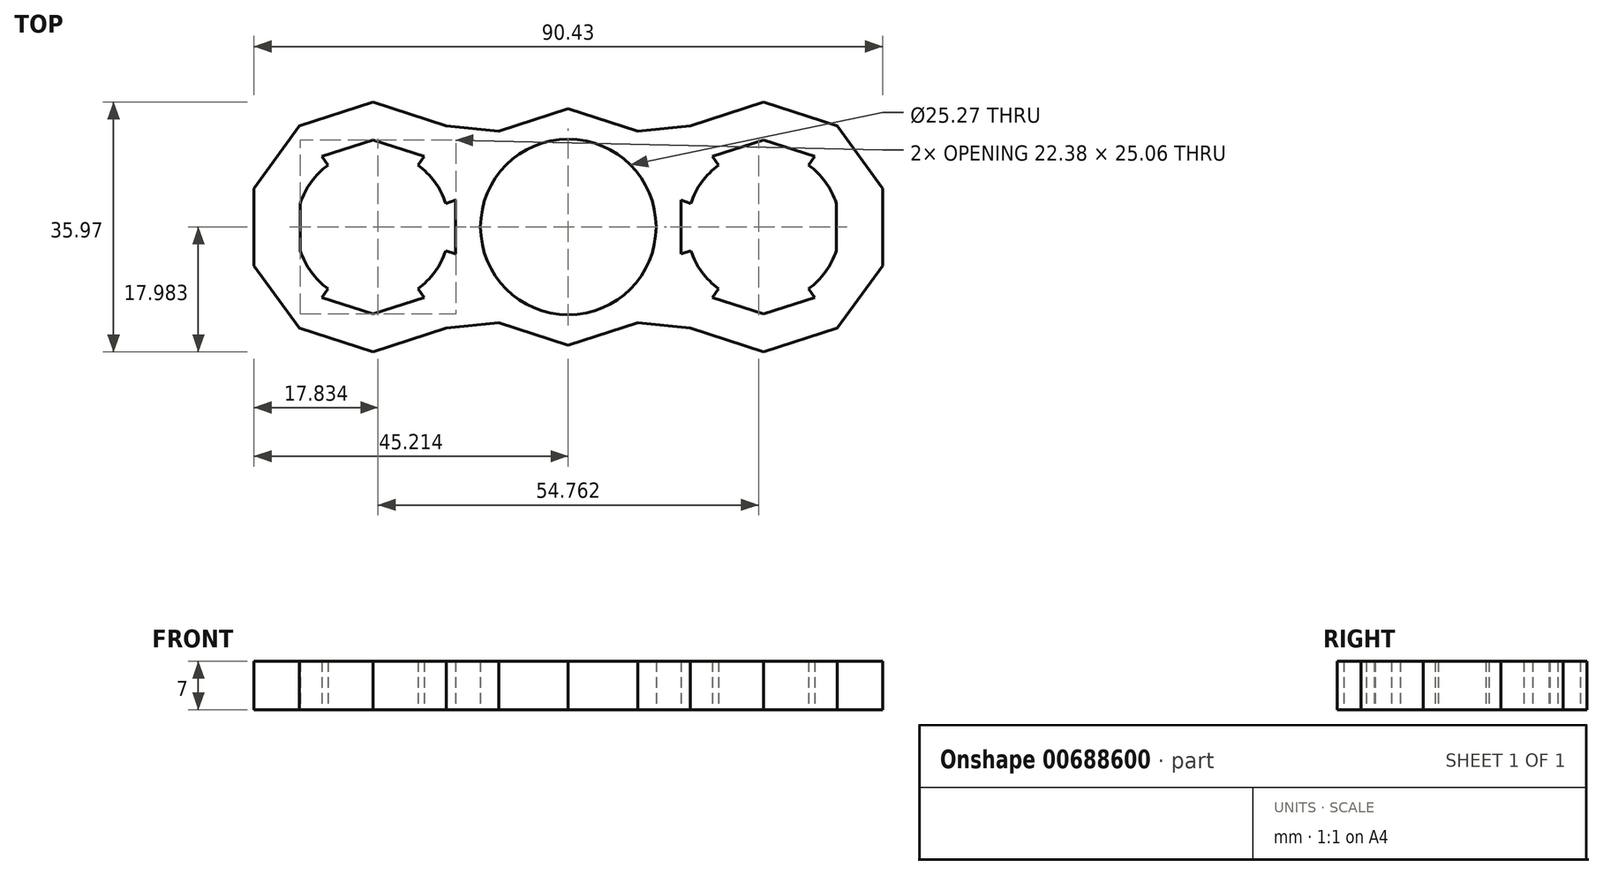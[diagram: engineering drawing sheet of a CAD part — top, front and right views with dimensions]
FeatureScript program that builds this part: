
annotation { "Feature Type Name" : "Feature", "Feature Type Description" : "" }
export const myFeature = defineFeature(function(context is Context, id is Id, definition is map)
    precondition{}
    {
        {
            var Q0;
            Q0=qCreatedBy(makeId("Top.planeOp"),FACE);
            var sketch = newSketch(context, id + "F0", { "sketchPlane" : qUnion([Q0])});
            skLineSegment(sketch, "E0.2", {"start": v(-42.82, -39.05) * mm, "end": v(-52.83, -42.3) * mm});
            skLineSegment(sketch, "E0.3", {"start": v(-52.83, -42.3) * mm, "end": v(-62.83, -39.05) * mm});
            skLineSegment(sketch, "E0.7", {"start": v(-62.83, -11.5) * mm, "end": v(-52.83, -8.25) * mm});
            skLineSegment(sketch, "E0.8", {"start": v(-52.83, -8.25) * mm, "end": v(-42.82, -11.5) * mm});
            skPoint(sketch, "E0.0.midPoint", {"position": v(-36.63, -25.28) * mm});
            skPoint(sketch, "E1.middle", {"position": v(-52.83, -25.28) * mm});
            skLineSegment(sketch, "E2.2", {"start": v(-70.36, -39.83) * mm, "end": v(-80.93, -43.26) * mm});
            skLineSegment(sketch, "E2.3", {"start": v(-80.93, -43.26) * mm, "end": v(-91.5, -39.83) * mm});
            skLineSegment(sketch, "E2.4", {"start": v(-91.5, -39.83) * mm, "end": v(-98.04, -30.84) * mm});
            skLineSegment(sketch, "E2.5", {"start": v(-98.04, -30.84) * mm, "end": v(-98.04, -19.72) * mm});
            skLineSegment(sketch, "E2.6", {"start": v(-98.04, -19.72) * mm, "end": v(-91.5, -10.72) * mm});
            skLineSegment(sketch, "E2.7", {"start": v(-91.5, -10.72) * mm, "end": v(-80.93, -7.29) * mm});
            skLineSegment(sketch, "E2.8", {"start": v(-80.93, -7.29) * mm, "end": v(-70.36, -10.72) * mm});
            skLineSegment(sketch, "E3.2", {"start": v(-35.3, -10.72) * mm, "end": v(-24.72, -7.29) * mm});
            skLineSegment(sketch, "E3.3", {"start": v(-24.72, -7.29) * mm, "end": v(-14.15, -10.72) * mm});
            skLineSegment(sketch, "E3.4", {"start": v(-14.15, -10.72) * mm, "end": v(-7.61, -19.72) * mm});
            skLineSegment(sketch, "E3.5", {"start": v(-7.61, -19.72) * mm, "end": v(-7.61, -30.84) * mm});
            skLineSegment(sketch, "E3.6", {"start": v(-7.61, -30.84) * mm, "end": v(-14.15, -39.83) * mm});
            skLineSegment(sketch, "E3.7", {"start": v(-14.15, -39.83) * mm, "end": v(-24.72, -43.26) * mm});
            skLineSegment(sketch, "E3.8", {"start": v(-24.72, -43.26) * mm, "end": v(-35.3, -39.83) * mm});
            skLineSegment(sketch, "E4", {"start": v(-42.82, -11.5) * mm, "end": v(-35.3, -10.72) * mm});
            skLineSegment(sketch, "E5", {"start": v(-70.36, -10.72) * mm, "end": v(-62.83, -11.5) * mm});
            skLineSegment(sketch, "E6", {"start": v(-70.36, -39.83) * mm, "end": v(-62.83, -39.05) * mm});
            skLineSegment(sketch, "E7", {"start": v(-42.82, -39.05) * mm, "end": v(-35.3, -39.83) * mm});
            skLineSegment(sketch, "E8.2", {"start": v(-73.57, -35.41) * mm, "end": v(-80.93, -37.8) * mm});
            skLineSegment(sketch, "E8.3", {"start": v(-80.93, -37.8) * mm, "end": v(-88.3, -35.41) * mm});
            skLineSegment(sketch, "E8.7", {"start": v(-88.3, -15.14) * mm, "end": v(-80.93, -12.75) * mm});
            skLineSegment(sketch, "E8.8", {"start": v(-80.93, -12.75) * mm, "end": v(-73.57, -15.14) * mm});
            skPoint(sketch, "E8.0.midPoint", {"position": v(-69.02, -25.28) * mm});
            skLineSegment(sketch, "E9", {"start": v(-70.47, -21.88) * mm, "end": v(-69.02, -21.4) * mm});
            skLineSegment(sketch, "E10", {"start": v(-70.47, -28.68) * mm, "end": v(-69.02, -29.15) * mm});
            skLineSegment(sketch, "E11.2", {"start": v(-32.08, -15.14) * mm, "end": v(-24.72, -12.75) * mm});
            skLineSegment(sketch, "E11.3", {"start": v(-24.72, -12.75) * mm, "end": v(-17.35, -15.14) * mm});
            skLineSegment(sketch, "E11.7", {"start": v(-17.35, -35.41) * mm, "end": v(-24.72, -37.8) * mm});
            skLineSegment(sketch, "E11.8", {"start": v(-24.72, -37.8) * mm, "end": v(-32.08, -35.41) * mm});
            skLineSegment(sketch, "E12", {"start": v(-36.63, -21.4) * mm, "end": v(-35.18, -21.88) * mm});
            skLineSegment(sketch, "E13", {"start": v(-36.63, -29.15) * mm, "end": v(-35.18, -28.68) * mm});
            skLineSegment(sketch, "E14", {"start": v(-69.02, -21.4) * mm, "end": v(-69.02, -29.15) * mm});
            skLineSegment(sketch, "E15", {"start": v(-74.47, -34.18) * mm, "end": v(-73.57, -35.41) * mm});
            skLineSegment(sketch, "E16", {"start": v(-87.4, -34.18) * mm, "end": v(-88.3, -35.41) * mm});
            skLineSegment(sketch, "E17", {"start": v(-87.4, -16.38) * mm, "end": v(-88.3, -15.14) * mm});
            skLineSegment(sketch, "E18", {"start": v(-74.47, -16.38) * mm, "end": v(-73.57, -15.14) * mm});
            skLineSegment(sketch, "E19", {"start": v(-36.63, -21.4) * mm, "end": v(-36.63, -29.15) * mm});
            skLineSegment(sketch, "E20", {"start": v(-32.08, -15.14) * mm, "end": v(-31.18, -16.38) * mm});
            skLineSegment(sketch, "E21", {"start": v(-17.35, -15.14) * mm, "end": v(-18.25, -16.38) * mm});
            skLineSegment(sketch, "E22", {"start": v(-18.25, -34.18) * mm, "end": v(-17.35, -35.41) * mm});
            skLineSegment(sketch, "E23", {"start": v(-31.18, -34.18) * mm, "end": v(-32.08, -35.41) * mm});
            skCircle(sketch, "E24", {"center": v(-52.83, -25.28) * mm, "radius": 12.64 * mm});
            skLineSegment(sketch, "E25.left", {"start": v(-98.04, -25.28) * mm, "end": v(-98.04, -25.28) * mm});
            skLineSegment(sketch, "E25.right", {"start": v(-7.61, -25.28) * mm, "end": v(-7.61, -25.28) * mm});
            skArc(sketch, "E26", {"start": v(-87.4, -16.38) * mm, "mid": v(-89.83, -18.81) * mm, "end": v(-91.4, -21.88) * mm});
            skArc(sketch, "E27", {"start": v(-35.18, -28.68) * mm, "mid": v(-33.62, -31.74) * mm, "end": v(-31.18, -34.18) * mm});
            skArc(sketch, "E28.trimOffspring", {"start": v(-70.47, -21.88) * mm, "mid": v(-72.03, -18.81) * mm, "end": v(-74.47, -16.38) * mm});
            skArc(sketch, "E29.trimOffspring", {"start": v(-74.47, -34.18) * mm, "mid": v(-72.03, -31.74) * mm, "end": v(-70.47, -28.68) * mm});
            skArc(sketch, "E30.trimOffspring", {"start": v(-91.4, -28.68) * mm, "mid": v(-89.83, -31.74) * mm, "end": v(-87.4, -34.18) * mm});
            skArc(sketch, "E31.trimOffspring", {"start": v(-31.18, -16.38) * mm, "mid": v(-33.62, -18.81) * mm, "end": v(-35.18, -21.88) * mm});
            skArc(sketch, "E32.trimOffspring", {"start": v(-18.25, -34.18) * mm, "mid": v(-15.82, -31.74) * mm, "end": v(-14.26, -28.68) * mm});
            skArc(sketch, "E33.trimOffspring", {"start": v(-14.26, -21.88) * mm, "mid": v(-15.82, -18.81) * mm, "end": v(-18.25, -16.38) * mm});
            skLineSegment(sketch, "E34", {"start": v(-91.4, -21.88) * mm, "end": v(-91.4, -28.68) * mm});
            skLineSegment(sketch, "E35", {"start": v(-14.26, -21.88) * mm, "end": v(-14.26, -28.68) * mm});
            skSolve(sketch);
        }
        {
            var Q0;
            Q0=makeQuery(id+"F0.imprint","IMPRINT",FACE,{"disambiguationData":[TD([[makeQuery(id+"F0.imprint","IMPRINT",EDGE,{"derivedFrom":sQuery(id+"F0.wireOp",EDGE,"E0.2")}),-1.0]])]});
            extrude(context, id + "F1", {"entities" : qUnion([Q0]), "depth" : 7 * mm, "offsetDistance" : 25.4 * mm});
        }
    });
